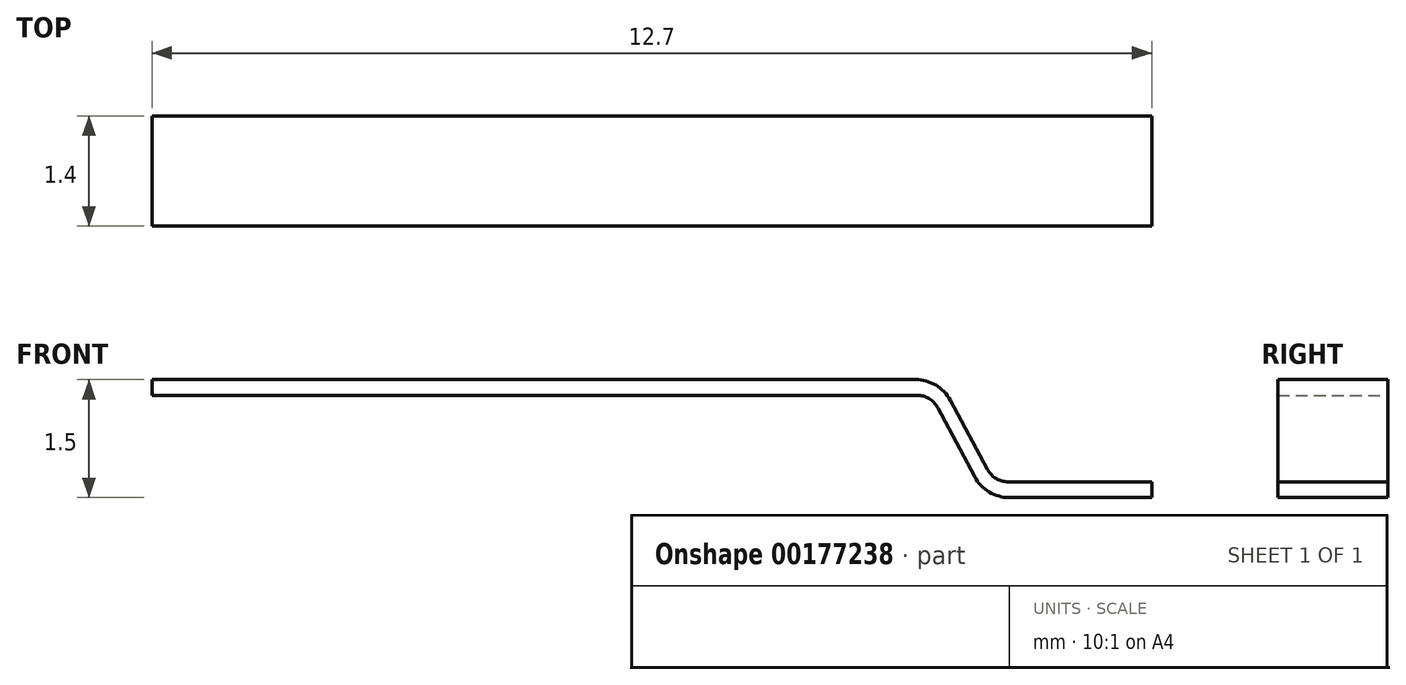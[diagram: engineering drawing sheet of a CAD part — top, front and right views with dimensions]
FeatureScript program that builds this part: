
annotation { "Feature Type Name" : "Feature", "Feature Type Description" : "" }
export const myFeature = defineFeature(function(context is Context, id is Id, definition is map)
    precondition{}
    {
        {
            var Q0;
            Q0=qCreatedBy(makeId("Front.planeOp"),FACE);
            var sketch = newSketch(context, id + "F0", { "sketchPlane" : qUnion([Q0])});
            skLineSegment(sketch, "E0.bottom", {"start": v(-5, 0.1) * mm, "end": v(5, 0.1) * mm});
            skLineSegment(sketch, "E0.top", {"start": v(-5, -0.1) * mm, "end": v(5, -0.1) * mm});
            skLineSegment(sketch, "E0.left", {"start": v(-5, 0.1) * mm, "end": v(-5, -0.1) * mm});
            skLineSegment(sketch, "E0.right", {"start": v(5, 0.1) * mm, "end": v(5, -0.1) * mm});
            skPoint(sketch, "E0.middle", {"position": v(0, 0) * mm});
            skLineSegment(sketch, "E1.bottom", {"start": v(5.7, -1.2) * mm, "end": v(7.7, -1.2) * mm});
            skLineSegment(sketch, "E1.top", {"start": v(5.7, -1.4) * mm, "end": v(7.7, -1.4) * mm});
            skLineSegment(sketch, "E1.left", {"start": v(5.7, -1.2) * mm, "end": v(5.7, -1.4) * mm});
            skLineSegment(sketch, "E1.right", {"start": v(7.7, -1.2) * mm, "end": v(7.7, -1.4) * mm});
            skLineSegment(sketch, "E2", {"start": v(5, 0.1) * mm, "end": v(5.7, -1.2) * mm});
            skLineSegment(sketch, "E3", {"start": v(4.9, -0.1) * mm, "end": v(5.6, -1.4) * mm});
            skLineSegment(sketch, "E4", {"start": v(5.7, -1.4) * mm, "end": v(5.6, -1.4) * mm});
            skSolve(sketch);
        }
        {
            var Q0;
            Q0=makeQuery(id+"F0.imprint","IMPRINT",FACE,{"disambiguationData":[TD([[makeQuery(id+"F0.imprint","IMPRINT",EDGE,{"derivedFrom":sQuery(id+"F0.wireOp",EDGE,"E0.bottom")}),-1.0]])]});
            var Q1;
            {var subQ0=sQuery(id+"F0.wireOp",EDGE,"E0.right");Q1=makeQuery(id+"F0.imprint","IMPRINT",FACE,{"disambiguationData":[TD([[makeQuery(id+"F0.imprint","IMPRINT",EDGE,{"derivedFrom":subQ0}),1.0]])]});}
            var Q2;
            Q2=makeQuery(id+"F0.imprint","IMPRINT",FACE,{"disambiguationData":[TD([[makeQuery(id+"F0.imprint","IMPRINT",EDGE,{"derivedFrom":sQuery(id+"F0.wireOp",EDGE,"E1.bottom")}),-1.0]])]});
            extrude(context, id + "F1", {"entities" : qUnion([Q0, Q1, Q2]), "depth" : 1.4 * mm});
        }
        {
            var Q0;
            Q0=makeQuery(id+"F1.opExtrude","SWEPT_EDGE",EDGE,{"disambiguationData":[OSD([sQuery(id+"F0.wireOp",EDGE,"E1.bottom"),sQuery(id+"F0.wireOp",EDGE,"E1.left"),sQuery(id+"F0.wireOp",EDGE,"E2")])]});
            var Q1;
            Q1=makeQuery(id+"F1.opExtrude","SWEPT_EDGE",EDGE,{"disambiguationData":[OSD([sQuery(id+"F0.wireOp",EDGE,"E0.top"),sQuery(id+"F0.wireOp",EDGE,"E3")])]});
            fillet(context, id + "F2", {"entities" : qUnion([Q0, Q1]), "radius" : 0.3 * mm, "tangentPropagation" : true, "allowEdgeOverflow" : false});
        }
        {
            var Q0;
            Q0=makeQuery(id+"F1.opExtrude","SWEPT_EDGE",EDGE,{"disambiguationData":[OSD([sQuery(id+"F0.wireOp",EDGE,"E0.bottom"),sQuery(id+"F0.wireOp",EDGE,"E0.right"),sQuery(id+"F0.wireOp",EDGE,"E2")])]});
            var Q1;
            Q1=makeQuery(id+"F1.opExtrude","SWEPT_EDGE",EDGE,{"disambiguationData":[OSD([sQuery(id+"F0.wireOp",EDGE,"E3"),sQuery(id+"F0.wireOp",EDGE,"E4")])]});
            fillet(context, id + "F3", {"entities" : qUnion([Q0, Q1]), "radius" : 0.5 * mm, "tangentPropagation" : true, "allowEdgeOverflow" : false});
        }
    });
